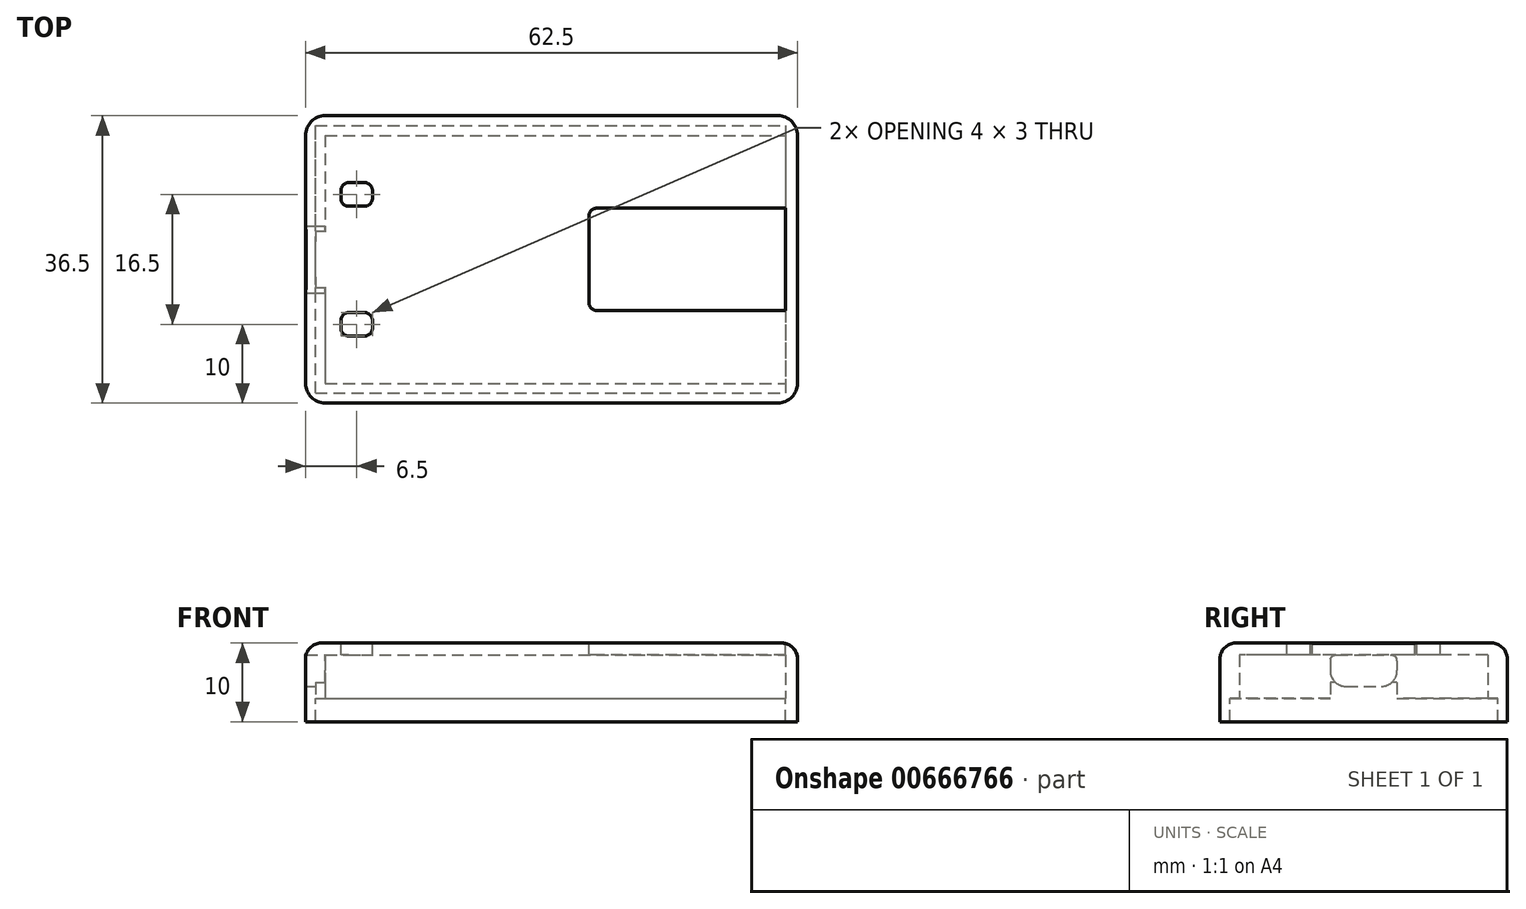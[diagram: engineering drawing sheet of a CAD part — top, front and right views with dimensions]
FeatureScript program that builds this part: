
annotation { "Feature Type Name" : "Feature", "Feature Type Description" : "" }
export const myFeature = defineFeature(function(context is Context, id is Id, definition is map)
    precondition{}
    {
        {
            var Q0;
            Q0=qCreatedBy(makeId("Top.planeOp"),FACE);
            var sketch = newSketch(context, id + "F0", { "sketchPlane" : qUnion([Q0])});
            skLineSegment(sketch, "E0.bottom", {"start": v(-30.75, 18.75) * mm, "end": v(31.75, 18.75) * mm});
            skLineSegment(sketch, "E0.top", {"start": v(-30.75, -17.75) * mm, "end": v(31.75, -17.75) * mm});
            skLineSegment(sketch, "E0.left", {"start": v(-30.75, 18.75) * mm, "end": v(-30.75, -17.75) * mm});
            skLineSegment(sketch, "E0.right", {"start": v(31.75, 18.75) * mm, "end": v(31.75, -17.75) * mm});
            skLineSegment(sketch, "E1.bottom", {"start": v(-28.25, 16.25) * mm, "end": v(30.25, 16.25) * mm});
            skLineSegment(sketch, "E1.top", {"start": v(-28.25, -15.25) * mm, "end": v(30.25, -15.25) * mm});
            skLineSegment(sketch, "E1.left", {"start": v(-28.25, 16.25) * mm, "end": v(-28.25, -15.25) * mm});
            skLineSegment(sketch, "E1.right", {"start": v(30.25, 16.25) * mm, "end": v(30.25, -15.25) * mm});
            skSolve(sketch);
        }
        {
            var Q0;
            Q0=makeQuery(id+"F0.imprint","IMPRINT",FACE,{"disambiguationData":[TD([[makeQuery(id+"F0.imprint","IMPRINT",EDGE,{"derivedFrom":sQuery(id+"F0.wireOp",EDGE,"E0.bottom")}),-1.0]])]});
            extrude(context, id + "F1", {"entities" : qUnion([Q0]), "depth" : 7 * mm});
        }
        {
            var Q0;
            Q0=makeQuery(id+"F1.opExtrude","CAP_FACE",FACE,{"disambiguationData":[OSD([sQuery(id+"F0.wireOp",EDGE,"E0.bottom"),sQuery(id+"F0.wireOp",EDGE,"E0.top"),sQuery(id+"F0.wireOp",EDGE,"E0.left"),sQuery(id+"F0.wireOp",EDGE,"E0.right"),sQuery(id+"F0.wireOp",EDGE,"E1.bottom"),sQuery(id+"F0.wireOp",EDGE,"E1.top"),sQuery(id+"F0.wireOp",EDGE,"E1.left"),sQuery(id+"F0.wireOp",EDGE,"E1.right")])],"isStart":false});
            var sketch = newSketch(context, id + "F2", { "sketchPlane" : qUnion([Q0])});
            skLineSegment(sketch, "E2.bottom", {"start": v(-28.25, 16.25) * mm, "end": v(30.25, 16.25) * mm});
            skLineSegment(sketch, "E2.top", {"start": v(-28.25, -15.25) * mm, "end": v(30.25, -15.25) * mm});
            skLineSegment(sketch, "E2.left", {"start": v(-28.25, 16.25) * mm, "end": v(-28.25, -15.25) * mm});
            skLineSegment(sketch, "E3.bottom", {"start": v(30.25, 7) * mm, "end": v(5.25, 7) * mm});
            skLineSegment(sketch, "E3.top", {"start": v(30.25, -6) * mm, "end": v(5.25, -6) * mm});
            skLineSegment(sketch, "E3.right", {"start": v(5.25, 7) * mm, "end": v(5.25, -6) * mm});
            skLineSegment(sketch, "E4.bottom", {"start": v(-26.25, 10.25) * mm, "end": v(-22.25, 10.25) * mm});
            skLineSegment(sketch, "E4.top", {"start": v(-26.25, 7.25) * mm, "end": v(-22.25, 7.25) * mm});
            skLineSegment(sketch, "E4.left", {"start": v(-26.25, 10.25) * mm, "end": v(-26.25, 7.25) * mm});
            skLineSegment(sketch, "E4.right", {"start": v(-22.25, 10.25) * mm, "end": v(-22.25, 7.25) * mm});
            skLineSegment(sketch, "E5.bottom", {"start": v(-26.25, -6.25) * mm, "end": v(-22.25, -6.25) * mm});
            skLineSegment(sketch, "E5.top", {"start": v(-26.25, -9.25) * mm, "end": v(-22.25, -9.25) * mm});
            skLineSegment(sketch, "E5.left", {"start": v(-26.25, -6.25) * mm, "end": v(-26.25, -9.25) * mm});
            skLineSegment(sketch, "E5.right", {"start": v(-22.25, -6.25) * mm, "end": v(-22.25, -9.25) * mm});
            skLineSegment(sketch, "E6", {"start": v(30.25, 16.25) * mm, "end": v(30.25, 7) * mm});
            skLineSegment(sketch, "E7", {"start": v(30.25, -6) * mm, "end": v(30.25, -15.25) * mm});
            skLineSegment(sketch, "E8.bottom", {"start": v(30.25, -6) * mm, "end": v(28.14, -6) * mm});
            skLineSegment(sketch, "E8.top", {"start": v(30.25, 7) * mm, "end": v(28.14, 7) * mm});
            skLineSegment(sketch, "E8.left", {"start": v(30.25, -6) * mm, "end": v(30.25, 7) * mm});
            skLineSegment(sketch, "E8.right", {"start": v(28.14, -6) * mm, "end": v(28.14, 7) * mm});
            skSolve(sketch);
        }
        {
            var Q0;
            Q0=makeQuery(id+"F2.imprint","IMPRINT",FACE,{"disambiguationData":[TD([[makeQuery(id+"F2.imprint","IMPRINT",EDGE,{"derivedFrom":sQuery(id+"F2.wireOp",EDGE,"E2.bottom")}),-1.0]])]});
            var Q1;
            Q1=makeQuery(id+"F2.imprint","IMPRINT",FACE,{"disambiguationData":[TD([[makeQuery(id+"F2.imprint","IMPRINT",EDGE,{"derivedFrom":sQuery(id+"F2.wireOp",EDGE,"E8.bottom")}),-1.0]])]});
            extrude(context, id + "F3", {"entities" : qUnion([Q0, Q1]), "operationType" : NewBodyOperationType.ADD, "oppositeDirection" : true, "depth" : 1.5 * mm, "offsetDistance" : 25 * mm});
        }
        {
            var Q0;
            Q0=makeQuery(id+"F1.opExtrude","CAP_FACE",FACE,{"disambiguationData":[OSD([sQuery(id+"F0.wireOp",EDGE,"E0.bottom"),sQuery(id+"F0.wireOp",EDGE,"E0.top"),sQuery(id+"F0.wireOp",EDGE,"E0.left"),sQuery(id+"F0.wireOp",EDGE,"E0.right"),sQuery(id+"F0.wireOp",EDGE,"E1.bottom"),sQuery(id+"F0.wireOp",EDGE,"E1.top"),sQuery(id+"F0.wireOp",EDGE,"E1.left"),sQuery(id+"F0.wireOp",EDGE,"E1.right")])],"isStart":true});
            var sketch = newSketch(context, id + "F4", { "sketchPlane" : qUnion([Q0])});
            skLineSegment(sketch, "E9.bottom", {"start": v(-30.75, 17.75) * mm, "end": v(31.75, 17.75) * mm});
            skLineSegment(sketch, "E9.top", {"start": v(-30.75, -18.75) * mm, "end": v(31.75, -18.75) * mm});
            skLineSegment(sketch, "E9.left", {"start": v(-30.75, 17.75) * mm, "end": v(-30.75, -18.75) * mm});
            skLineSegment(sketch, "E9.right", {"start": v(31.75, 17.75) * mm, "end": v(31.75, -18.75) * mm});
            skLineSegment(sketch, "E10.bottom", {"start": v(-29.5, 16.5) * mm, "end": v(30.25, 16.5) * mm});
            skLineSegment(sketch, "E10.top", {"start": v(-29.5, -17.52) * mm, "end": v(30.25, -17.52) * mm});
            skLineSegment(sketch, "E10.left", {"start": v(-29.5, 16.5) * mm, "end": v(-29.5, -17.52) * mm});
            skLineSegment(sketch, "E10.right", {"start": v(30.25, 16.5) * mm, "end": v(30.25, -17.52) * mm});
            skSolve(sketch);
        }
        {
            var Q0;
            Q0=makeQuery(id+"F4.imprint","IMPRINT",FACE,{"disambiguationData":[TD([[makeQuery(id+"F4.imprint","IMPRINT",EDGE,{"derivedFrom":sQuery(id+"F4.wireOp",EDGE,"E9.bottom")}),-1.0]])]});
            var Q1;
            {var subQ5=makeQuery(id+"F1.opExtrude","CAP_EDGE",EDGE,{"disambiguationData":[OSD([sQuery(id+"F0.wireOp",EDGE,"E1.right")])],"isStart":true});Q1=makeQuery(id+"F4.imprint","IMPRINT",FACE,{"disambiguationData":[TD([[makeQuery(id+"F4.imprint","IMPRINT",EDGE,{"derivedFrom":subQ5}),1.0]])]});}
            extrude(context, id + "F5", {"entities" : qUnion([Q0, Q1]), "operationType" : NewBodyOperationType.ADD, "depth" : 3 * mm});
        }
        {
            var Q0;
            Q0=makeQuery(id+"F1.opExtrude","SWEPT_FACE",FACE,{"disambiguationData":[OSD([sQuery(id+"F0.wireOp",EDGE,"E1.left")])]});
            var sketch = newSketch(context, id + "F6", { "sketchPlane" : qUnion([Q0])});
            skLineSegment(sketch, "E11.bottom", {"start": v(-3, 5.5) * mm, "end": v(4, 5.5) * mm});
            skLineSegment(sketch, "E11.top", {"start": v(-1.75, 1.5) * mm, "end": v(2.75, 1.5) * mm});
            skLineSegment(sketch, "E11.left", {"start": v(-3.75, 4.75) * mm, "end": v(-3.75, 3.5) * mm});
            skLineSegment(sketch, "E11.right", {"start": v(4.75, 4.75) * mm, "end": v(4.75, 3.5) * mm});
            skPoint(sketch, "E12.visualSharp", {"position": v(-3.75, 1.5) * mm});
            skArc(sketch, "E12.filletArc", {"start": v(-3.75, 3.5) * mm, "mid": v(-3.16, 2.09) * mm, "end": v(-1.75, 1.5) * mm});
            skPoint(sketch, "E13.visualSharp", {"position": v(4.75, 1.5) * mm});
            skArc(sketch, "E13.filletArc", {"start": v(2.75, 1.5) * mm, "mid": v(4.16, 2.09) * mm, "end": v(4.75, 3.5) * mm});
            skPoint(sketch, "E14.visualSharp", {"position": v(4.75, 5.5) * mm});
            skArc(sketch, "E14.filletArc", {"start": v(4.75, 4.75) * mm, "mid": v(4.53, 5.28) * mm, "end": v(4, 5.5) * mm});
            skPoint(sketch, "E15.visualSharp", {"position": v(-3.75, 5.5) * mm});
            skArc(sketch, "E15.filletArc", {"start": v(-3, 5.5) * mm, "mid": v(-3.53, 5.28) * mm, "end": v(-3.75, 4.75) * mm});
            skSolve(sketch);
        }
        {
            var Q0;
            Q0=makeQuery(id+"F6.imprint","IMPRINT",FACE,{"disambiguationData":[TD([[makeQuery(id+"F6.imprint","IMPRINT",EDGE,{"derivedFrom":sQuery(id+"F6.wireOp",EDGE,"E11.bottom")}),1.0]])]});
            extrude(context, id + "F7", {"entities" : qUnion([Q0]), "operationType" : NewBodyOperationType.REMOVE, "oppositeDirection" : true, "depth" : 2.5 * mm});
        }
        {
            var Q0;
            Q0=makeQuery(id+"F5.boolean.opBoolean","MERGE",EDGE,{"derivedFrom":[makeQuery(id+"F1.opExtrude","SWEPT_EDGE",EDGE,{"disambiguationData":[OSD([sQuery(id+"F0.wireOp",EDGE,"E0.bottom"),sQuery(id+"F0.wireOp",EDGE,"E0.left")])]}),makeQuery(id+"F5.opExtrude","SWEPT_EDGE",EDGE,{"disambiguationData":[OSD([sQuery(id+"F4.wireOp",EDGE,"E9.top"),sQuery(id+"F4.wireOp",EDGE,"E9.left")])]})]});
            var Q1;
            Q1=makeQuery(id+"F5.boolean.opBoolean","MERGE",EDGE,{"derivedFrom":[makeQuery(id+"F1.opExtrude","SWEPT_EDGE",EDGE,{"disambiguationData":[OSD([sQuery(id+"F0.wireOp",EDGE,"E0.top"),sQuery(id+"F0.wireOp",EDGE,"E0.left")])]}),makeQuery(id+"F5.opExtrude","SWEPT_EDGE",EDGE,{"disambiguationData":[OSD([sQuery(id+"F4.wireOp",EDGE,"E9.bottom"),sQuery(id+"F4.wireOp",EDGE,"E9.left")])]})]});
            var Q2;
            Q2=makeQuery(id+"F5.boolean.opBoolean","MERGE",EDGE,{"derivedFrom":[makeQuery(id+"F1.opExtrude","SWEPT_EDGE",EDGE,{"disambiguationData":[OSD([sQuery(id+"F0.wireOp",EDGE,"E0.bottom"),sQuery(id+"F0.wireOp",EDGE,"E0.right")])]}),makeQuery(id+"F5.opExtrude","SWEPT_EDGE",EDGE,{"disambiguationData":[OSD([sQuery(id+"F4.wireOp",EDGE,"E9.top"),sQuery(id+"F4.wireOp",EDGE,"E9.right")])]})]});
            var Q3;
            Q3=makeQuery(id+"F5.boolean.opBoolean","MERGE",EDGE,{"derivedFrom":[makeQuery(id+"F1.opExtrude","SWEPT_EDGE",EDGE,{"disambiguationData":[OSD([sQuery(id+"F0.wireOp",EDGE,"E0.top"),sQuery(id+"F0.wireOp",EDGE,"E0.right")])]}),makeQuery(id+"F5.opExtrude","SWEPT_EDGE",EDGE,{"disambiguationData":[OSD([sQuery(id+"F4.wireOp",EDGE,"E9.bottom"),sQuery(id+"F4.wireOp",EDGE,"E9.right")])]})]});
            fillet(context, id + "F8", {"entities" : qUnion([Q0, Q1, Q2, Q3]), "radius" : 2.5 * mm, "tangentPropagation" : true, "allowEdgeOverflow" : false});
        }
        {
            var Q0;
            Q0=makeQuery(id+"F3.opExtrude","SWEPT_EDGE",EDGE,{"disambiguationData":[OSD([sQuery(id+"F2.wireOp",EDGE,"E3.bottom"),sQuery(id+"F2.wireOp",EDGE,"E3.right")])]});
            var Q1;
            Q1=makeQuery(id+"F3.opExtrude","SWEPT_EDGE",EDGE,{"disambiguationData":[OSD([sQuery(id+"F0.wireOp",EDGE,"E1.right"),sQuery(id+"F2.wireOp",EDGE,"E3.bottom"),sQuery(id+"F2.wireOp",EDGE,"E6")])]});
            var Q2;
            Q2=makeQuery(id+"F3.opExtrude","SWEPT_EDGE",EDGE,{"disambiguationData":[OSD([sQuery(id+"F0.wireOp",EDGE,"E1.right"),sQuery(id+"F2.wireOp",EDGE,"E3.top"),sQuery(id+"F2.wireOp",EDGE,"E7")])]});
            var Q3;
            Q3=makeQuery(id+"F3.opExtrude","SWEPT_EDGE",EDGE,{"disambiguationData":[OSD([sQuery(id+"F2.wireOp",EDGE,"E3.top"),sQuery(id+"F2.wireOp",EDGE,"E3.right")])]});
            fillet(context, id + "F9", {"entities" : qUnion([Q0, Q1, Q2, Q3]), "radius" : 1 * mm, "tangentPropagation" : true, "allowEdgeOverflow" : false});
        }
        {
            var Q0;
            Q0=makeQuery(id+"F3.opExtrude","SWEPT_EDGE",EDGE,{"disambiguationData":[OSD([sQuery(id+"F2.wireOp",EDGE,"E4.bottom"),sQuery(id+"F2.wireOp",EDGE,"E4.right")])]});
            var Q1;
            Q1=makeQuery(id+"F3.opExtrude","SWEPT_EDGE",EDGE,{"disambiguationData":[OSD([sQuery(id+"F2.wireOp",EDGE,"E4.bottom"),sQuery(id+"F2.wireOp",EDGE,"E4.left")])]});
            var Q2;
            Q2=makeQuery(id+"F3.opExtrude","SWEPT_EDGE",EDGE,{"disambiguationData":[OSD([sQuery(id+"F2.wireOp",EDGE,"E4.top"),sQuery(id+"F2.wireOp",EDGE,"E4.left")])]});
            var Q3;
            Q3=makeQuery(id+"F3.opExtrude","SWEPT_EDGE",EDGE,{"disambiguationData":[OSD([sQuery(id+"F2.wireOp",EDGE,"E4.top"),sQuery(id+"F2.wireOp",EDGE,"E4.right")])]});
            var Q4;
            Q4=makeQuery(id+"F3.opExtrude","SWEPT_EDGE",EDGE,{"disambiguationData":[OSD([sQuery(id+"F2.wireOp",EDGE,"E5.bottom"),sQuery(id+"F2.wireOp",EDGE,"E5.left")])]});
            var Q5;
            Q5=makeQuery(id+"F3.opExtrude","SWEPT_EDGE",EDGE,{"disambiguationData":[OSD([sQuery(id+"F2.wireOp",EDGE,"E5.bottom"),sQuery(id+"F2.wireOp",EDGE,"E5.right")])]});
            var Q6;
            Q6=makeQuery(id+"F3.opExtrude","SWEPT_EDGE",EDGE,{"disambiguationData":[OSD([sQuery(id+"F2.wireOp",EDGE,"E5.top"),sQuery(id+"F2.wireOp",EDGE,"E5.right")])]});
            var Q7;
            Q7=makeQuery(id+"F3.opExtrude","SWEPT_EDGE",EDGE,{"disambiguationData":[OSD([sQuery(id+"F2.wireOp",EDGE,"E5.top"),sQuery(id+"F2.wireOp",EDGE,"E5.left")])]});
            fillet(context, id + "F10", {"entities" : qUnion([Q0, Q1, Q2, Q3, Q4, Q5, Q6, Q7]), "radius" : 1 * mm, "tangentPropagation" : true, "allowEdgeOverflow" : false});
        }
        {
            var Q0;
            Q0=makeQuery(id+"F1.opExtrude","CAP_EDGE",EDGE,{"disambiguationData":[OSD([sQuery(id+"F0.wireOp",EDGE,"E0.top")])],"isStart":false});
            fillet(context, id + "F11", {"entities" : qUnion([Q0]), "radius" : 2 * mm, "tangentPropagation" : true, "allowEdgeOverflow" : false});
        }
        {
            var Q0;
            Q0=makeQuery(id+"F1.opExtrude","CAP_FACE",FACE,{"disambiguationData":[OSD([sQuery(id+"F0.wireOp",EDGE,"E0.bottom"),sQuery(id+"F0.wireOp",EDGE,"E0.top"),sQuery(id+"F0.wireOp",EDGE,"E0.left"),sQuery(id+"F0.wireOp",EDGE,"E0.right"),sQuery(id+"F0.wireOp",EDGE,"E1.bottom"),sQuery(id+"F0.wireOp",EDGE,"E1.top"),sQuery(id+"F0.wireOp",EDGE,"E1.left"),sQuery(id+"F0.wireOp",EDGE,"E1.right")])],"isStart":true});
            var sketch = newSketch(context, id + "F12", { "sketchPlane" : qUnion([Q0])});
            skLineSegment(sketch, "E16.bottom", {"start": v(-29.5, 3.75) * mm, "end": v(-28.25, 3.75) * mm});
            skLineSegment(sketch, "E16.top", {"start": v(-29.5, -4.75) * mm, "end": v(-28.25, -4.75) * mm});
            skLineSegment(sketch, "E16.left", {"start": v(-29.5, 3.75) * mm, "end": v(-29.5, -4.75) * mm});
            skLineSegment(sketch, "E16.right", {"start": v(-28.25, 3.75) * mm, "end": v(-28.25, -4.75) * mm});
            skSolve(sketch);
        }
        {
            var Q0;
            Q0=makeQuery(id+"F12.imprint","IMPRINT",FACE,{"disambiguationData":[TD([[makeQuery(id+"F12.imprint","IMPRINT",EDGE,{"derivedFrom":sQuery(id+"F12.wireOp",EDGE,"E16.bottom")}),-1.0]])]});
            extrude(context, id + "F13", {"entities" : qUnion([Q0]), "operationType" : NewBodyOperationType.REMOVE, "oppositeDirection" : true, "depth" : 2 * mm});
        }
    });
